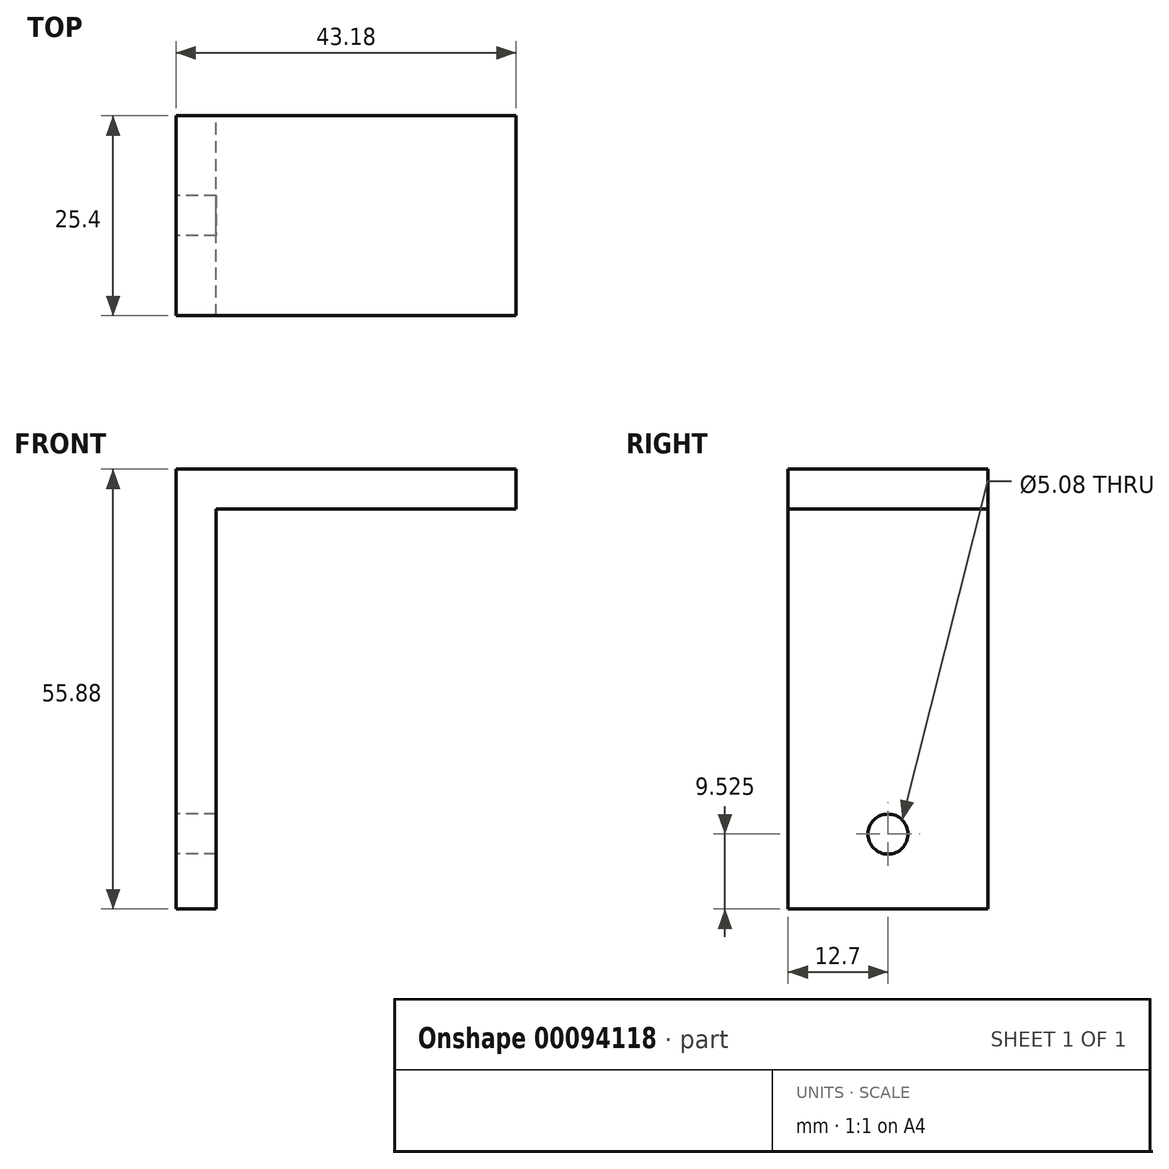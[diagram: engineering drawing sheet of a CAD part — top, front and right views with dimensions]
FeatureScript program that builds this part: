
annotation { "Feature Type Name" : "Feature", "Feature Type Description" : "" }
export const myFeature = defineFeature(function(context is Context, id is Id, definition is map)
    precondition{}
    {
        {
            var Q0;
            Q0=qCreatedBy(makeId("Front.planeOp"),FACE);
            var sketch = newSketch(context, id + "F0", { "sketchPlane" : qUnion([Q0])});
            skLineSegment(sketch, "E0.bottom", {"start": v(0, 0) * mm, "end": v(5.08, 0) * mm});
            skLineSegment(sketch, "E0.top", {"start": v(0, 55.88) * mm, "end": v(5.08, 55.88) * mm});
            skLineSegment(sketch, "E0.left", {"start": v(0, 0) * mm, "end": v(0, 55.88) * mm});
            skLineSegment(sketch, "E0.right", {"start": v(5.08, 0) * mm, "end": v(5.08, 55.88) * mm});
            skLineSegment(sketch, "E1.bottom", {"start": v(5.08, 55.88) * mm, "end": v(43.18, 55.88) * mm});
            skLineSegment(sketch, "E1.top", {"start": v(5.08, 50.8) * mm, "end": v(43.18, 50.8) * mm});
            skLineSegment(sketch, "E1.left", {"start": v(5.08, 55.88) * mm, "end": v(5.08, 50.8) * mm});
            skLineSegment(sketch, "E1.right", {"start": v(43.18, 55.88) * mm, "end": v(43.18, 50.8) * mm});
            skSolve(sketch);
        }
        {
            var Q0;
            Q0=makeQuery(id+"F0.imprint","IMPRINT",FACE,{"disambiguationData":[TD([[makeQuery(id+"F0.imprint","IMPRINT",EDGE,{"derivedFrom":sQuery(id+"F0.wireOp",EDGE,"E1.bottom")}),-1.0]])]});
            var Q1;
            Q1=makeQuery(id+"F0.imprint","IMPRINT",FACE,{"disambiguationData":[TD([[makeQuery(id+"F0.imprint","IMPRINT",EDGE,{"derivedFrom":sQuery(id+"F0.wireOp",EDGE,"E0.bottom")}),1.0]])]});
            extrude(context, id + "F1", {"entities" : qUnion([Q0, Q1]), "depth" : 25.4 * mm});
        }
        {
            var Q0;
            Q0=makeQuery(id+"F1.opExtrude","SWEPT_FACE",FACE,{"disambiguationData":[OSD([sQuery(id+"F0.wireOp",EDGE,"E0.left")])]});
            var sketch = newSketch(context, id + "F2", { "sketchPlane" : qUnion([Q0])});
            skCircle(sketch, "E2", {"center": v(12.7, 9.53) * mm, "radius": 2.54 * mm});
            skLineSegment(sketch, "E3", {"start": v(12.7, 55.88) * mm, "end": v(12.7, 0) * mm, "construction": true});
            skSolve(sketch);
        }
        {
            var Q0;
            Q0=makeQuery(id+"F2.imprint","IMPRINT",FACE,{"disambiguationData":[TD([[makeQuery(id+"F2.imprint","IMPRINT",EDGE,{"derivedFrom":sQuery(id+"F2.wireOp",EDGE,"E2")}),1.0]])]});
            extrude(context, id + "F3", {"entities" : qUnion([Q0]), "operationType" : NewBodyOperationType.REMOVE, "oppositeDirection" : true, "depth" : 25.4 * mm});
        }
    });
